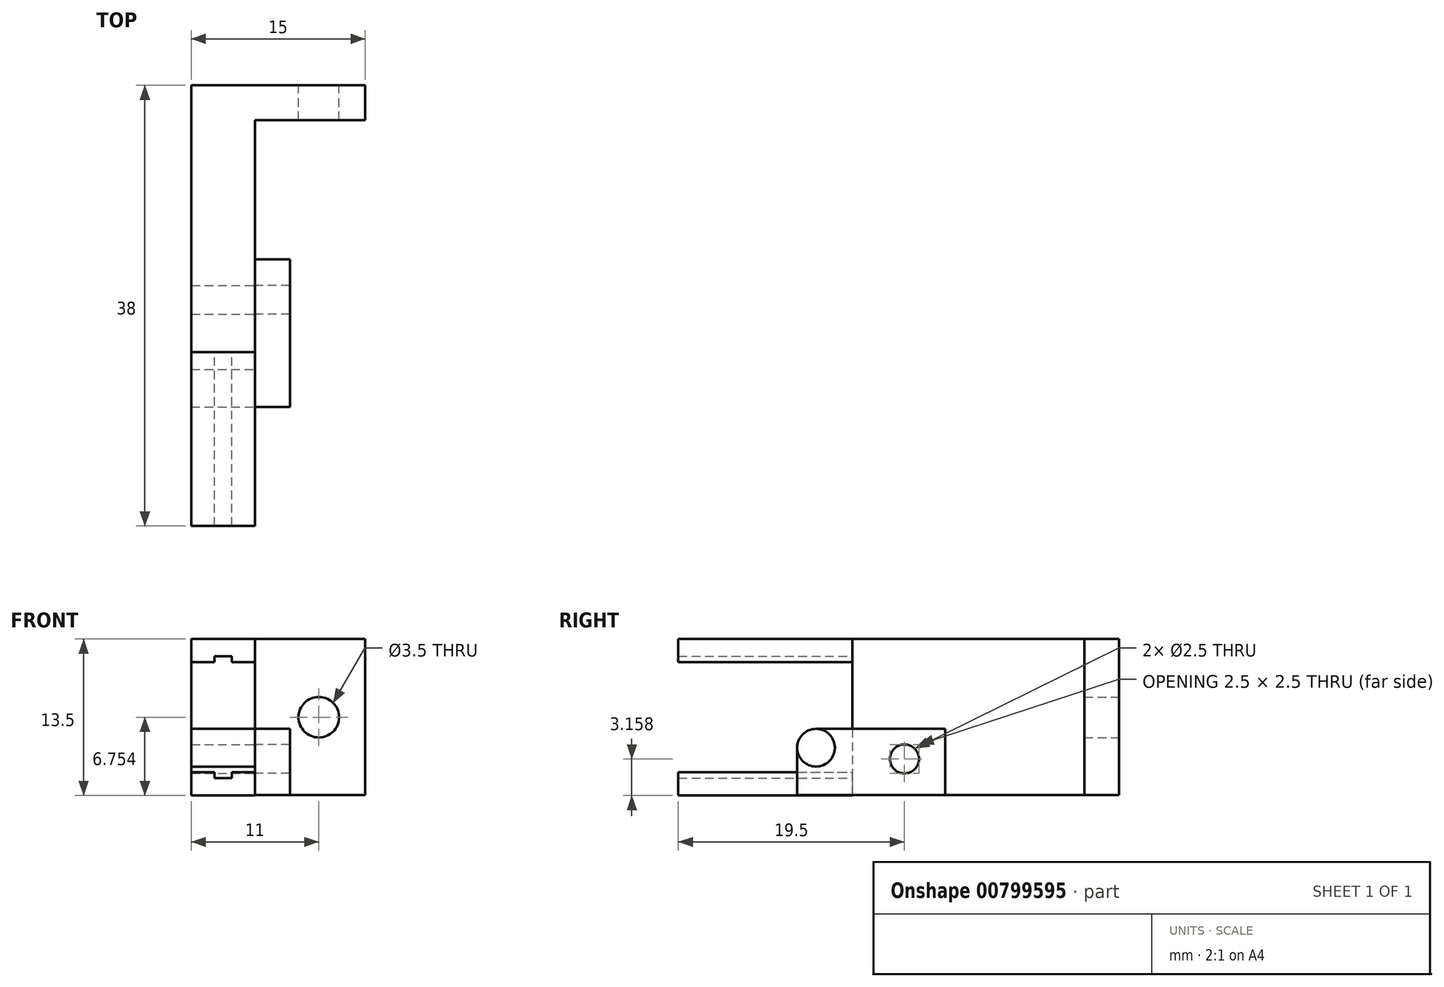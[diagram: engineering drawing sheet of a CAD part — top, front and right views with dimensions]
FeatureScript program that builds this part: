
annotation { "Feature Type Name" : "Feature", "Feature Type Description" : "" }
export const myFeature = defineFeature(function(context is Context, id is Id, definition is map)
    precondition{}
    {
        {
            var Q0;
            Q0=qCreatedBy(makeId("Right.planeOp"),FACE);
            cPlane(context, id + "F0", {"entities" : qUnion([Q0]), "cplaneType" : CPlaneType.OFFSET, "offset" : 2.75 * mm, "width" : 150 * mm, "height" : 150 * mm});
        }
        {
            var Q0;
            Q0=qCreatedBy(makeId("Front.planeOp"),FACE);
            var sketch = newSketch(context, id + "F1", { "sketchPlane" : qUnion([Q0])});
            skLineSegment(sketch, "E0", {"start": v(-0.75, 8) * mm, "end": v(-0.75, 7.5) * mm});
            skLineSegment(sketch, "E1", {"start": v(-0.75, 7.5) * mm, "end": v(-2.75, 7.5) * mm});
            skLineSegment(sketch, "E2", {"start": v(-2.75, 7.5) * mm, "end": v(-2.75, 9.5) * mm});
            skLineSegment(sketch, "E3", {"start": v(-2.75, 9.5) * mm, "end": v(2.75, 9.5) * mm});
            skLineSegment(sketch, "E4", {"start": v(2.75, 9.5) * mm, "end": v(2.75, 7.5) * mm});
            skLineSegment(sketch, "E5", {"start": v(2.75, 7.5) * mm, "end": v(0.75, 7.5) * mm});
            skLineSegment(sketch, "E6", {"start": v(0.75, 7.5) * mm, "end": v(0.75, 8) * mm});
            skLineSegment(sketch, "E7", {"start": v(0.75, 8) * mm, "end": v(-0.75, 8) * mm});
            skLineSegment(sketch, "E8.MirrorCS", {"start": v(0.75, -2.5) * mm, "end": v(-0.75, -2.5) * mm});
            skLineSegment(sketch, "E9.MirrorCS", {"start": v(0.75, -2) * mm, "end": v(0.75, -2.5) * mm});
            skLineSegment(sketch, "E10.MirrorCS", {"start": v(2.75, -4) * mm, "end": v(2.75, -2) * mm});
            skLineSegment(sketch, "E11.MirrorCS", {"start": v(-2.75, -4) * mm, "end": v(2.75, -4) * mm});
            skLineSegment(sketch, "E12.MirrorCS", {"start": v(2.75, -2) * mm, "end": v(0.75, -2) * mm});
            skLineSegment(sketch, "E13.MirrorCS", {"start": v(-0.75, -2.5) * mm, "end": v(-0.75, -2) * mm});
            skLineSegment(sketch, "E14.MirrorCS", {"start": v(-2.75, -2) * mm, "end": v(-2.75, -4) * mm});
            skLineSegment(sketch, "E15.MirrorCS", {"start": v(-0.75, -2) * mm, "end": v(-2.75, -2) * mm});
            skSolve(sketch);
        }
        {
            var Q0;
            Q0 = qSketchRegion(id + "F1", true);
            extrude(context, id + "F2", {"entities" : qUnion([Q0]), "depth" : 15 * mm, "offsetDistance" : 25 * mm});
        }
        {
            var Q0;
            Q0=qCreatedBy(makeId("Front.planeOp"),FACE);
            var sketch = newSketch(context, id + "F3", { "sketchPlane" : qUnion([Q0])});
            skLineSegment(sketch, "E16.bottom", {"start": v(-2.74, 9.5) * mm, "end": v(2.75, 9.5) * mm});
            skLineSegment(sketch, "E16.top", {"start": v(-2.74, -3.96) * mm, "end": v(2.75, -3.96) * mm});
            skLineSegment(sketch, "E16.left", {"start": v(-2.74, 9.5) * mm, "end": v(-2.74, -3.96) * mm});
            skLineSegment(sketch, "E16.right", {"start": v(2.75, 9.5) * mm, "end": v(2.75, -3.96) * mm});
            skSolve(sketch);
        }
        {
            var Q0;
            Q0 = qSketchRegion(id + "F3", true);
            extrude(context, id + "F4", {"entities" : qUnion([Q0]), "oppositeDirection" : true, "depth" : 20 * mm, "offsetDistance" : 25 * mm});
        }
        {
            var Q0;
            Q0=qCreatedBy(id+"F0.planeOp",FACE);
            var sketch = newSketch(context, id + "F5", { "sketchPlane" : qUnion([Q0])});
            skCircle(sketch, "E17", {"center": v(-3.12, 0.12) * mm, "radius": 1.63 * mm});
            skLineSegment(sketch, "E18.bottom", {"start": v(-3.12, 1.75) * mm, "end": v(8, 1.75) * mm});
            skLineSegment(sketch, "E18.top", {"start": v(-4.75, -3.96) * mm, "end": v(8, -3.96) * mm});
            skLineSegment(sketch, "E18.left", {"start": v(-4.75, 0.12) * mm, "end": v(-4.75, -3.96) * mm});
            skLineSegment(sketch, "E18.right", {"start": v(8, 1.75) * mm, "end": v(8, -3.96) * mm});
            skPoint(sketch, "E19.visualSharp", {"position": v(-4.75, 1.75) * mm});
            skArc(sketch, "E19.filletArc", {"start": v(-3.12, 1.75) * mm, "mid": v(-4.27, 1.27) * mm, "end": v(-4.75, 0.12) * mm});
            skPoint(sketch, "E20", {"position": v(4.5, -0.84) * mm});
            skSolve(sketch);
        }
        {
            var Q0;
            Q0=sQuery(id+"F5.wireOp",VERTEX,"E20");
            var Q1;
            Q1=makeQuery(id+"F4.opExtrude","SWEPT_BODY",BODY,{"disambiguationData":[OSD([sQuery(id+"F3.wireOp",EDGE,"E16.bottom"),sQuery(id+"F3.wireOp",EDGE,"E16.top"),sQuery(id+"F3.wireOp",EDGE,"E16.left"),sQuery(id+"F3.wireOp",EDGE,"E16.right")])]});
            hole(context, id + "F6", {"style" : HoleStyle.SIMPLE, "endStyle" : HoleEndStyle.THROUGH, "holeDiameter" : 2.5 * mm, "majorDiameter" : 5 * mm, "isTappedThrough" : true, "tappedDepth" : 12 * mm, "tapClearance" : 3, "locations" : qUnion([Q0]), "scope" : qUnion([Q1])});
        }
        {
            var Q0;
            {var subQ0=sQuery(id+"F5.wireOp",EDGE,"E17");var subQ1=makeQuery(id+"F5.imprint","INTERSECT",VERTEX,{"derivedFrom":[subQ0,sQuery(id+"F5.wireOp",EDGE,"E18.bottom")]});Q0=makeQuery(id+"F5.imprint","IMPRINT",FACE,{"disambiguationData":[TD([[makeQuery(id+"F5.imprint","IMPRINT",EDGE,{"disambiguationData":[TD([[subQ1,-1.0]])],"derivedFrom":subQ0}),1.0]])]});}
            extrude(context, id + "F7", {"entities" : qUnion([Q0]), "depth" : -5.5 * mm, "offsetDistance" : 25 * mm});
        }
        {
            var Q0;
            Q0 = qSketchRegion(id + "F5", true);
            extrude(context, id + "F8", {"entities" : qUnion([Q0]), "depth" : 3 * mm, "offsetDistance" : 25 * mm});
        }
        {
            var Q0;
            Q0=sQuery(id+"F5.wireOp",VERTEX,"E20");
            var Q1;
            Q1=makeQuery(id+"F8.opExtrude","SWEPT_BODY",BODY,{"disambiguationData":[OSD([sQuery(id+"F5.wireOp",EDGE,"E17"),sQuery(id+"F5.wireOp",EDGE,"E18.bottom"),sQuery(id+"F5.wireOp",EDGE,"E18.top"),sQuery(id+"F5.wireOp",EDGE,"E18.left"),sQuery(id+"F5.wireOp",EDGE,"E18.right")])]});
            hole(context, id + "F9", {"style" : HoleStyle.SIMPLE, "endStyle" : HoleEndStyle.THROUGH, "oppositeDirection" : true, "holeDiameter" : 2.5 * mm, "majorDiameter" : 5 * mm, "isTappedThrough" : true, "tappedDepth" : 12 * mm, "tapClearance" : 3, "locations" : qUnion([Q0]), "scope" : qUnion([Q1])});
        }
        {
            var Q0;
            Q0=qCreatedBy(makeId("Right.planeOp"),FACE);
            cPlane(context, id + "F10", {"entities" : qUnion([Q0]), "cplaneType" : CPlaneType.OFFSET, "offset" : 2.75 * mm, "oppositeDirection" : true, "width" : 150 * mm, "height" : 150 * mm});
        }
        {
            var Q0;
            Q0=qCreatedBy(id+"F10.planeOp",FACE);
            var sketch = newSketch(context, id + "F11", { "sketchPlane" : qUnion([Q0])});
            skLineSegment(sketch, "E21.bottom", {"start": v(20, 9.5) * mm, "end": v(23, 9.5) * mm});
            skLineSegment(sketch, "E21.top", {"start": v(20, -3.96) * mm, "end": v(23, -3.96) * mm});
            skLineSegment(sketch, "E21.left", {"start": v(20, 9.5) * mm, "end": v(20, -3.96) * mm});
            skLineSegment(sketch, "E21.right", {"start": v(23, 9.5) * mm, "end": v(23, -3.96) * mm});
            skSolve(sketch);
        }
        {
            var Q0;
            Q0 = qSketchRegion(id + "F11", true);
            extrude(context, id + "F12", {"entities" : qUnion([Q0]), "operationType" : NewBodyOperationType.ADD, "depth" : 15 * mm, "offsetDistance" : 25 * mm});
        }
        {
            var Q0;
            Q0=makeQuery(id+"F12.opExtrude","SWEPT_FACE",FACE,{"disambiguationData":[OSD([sQuery(id+"F11.wireOp",EDGE,"E21.right")])]});
            cPlane(context, id + "F13", {"entities" : qUnion([Q0]), "cplaneType" : CPlaneType.OFFSET, "offset" : 0 * mm, "width" : 150 * mm, "height" : 150 * mm});
        }
        {
            var Q0;
            Q0=qCreatedBy(id+"F13.planeOp",FACE);
            var sketch = newSketch(context, id + "F14", { "sketchPlane" : qUnion([Q0])});
            skPoint(sketch, "E22", {"position": v(-8.25, 2.75) * mm});
            skSolve(sketch);
        }
        {
            var Q0;
            Q0=sQuery(id+"F14.wireOp",VERTEX,"E22");
            var Q1;
            Q1=makeQuery(id+"F4.opExtrude","SWEPT_BODY",BODY,{"disambiguationData":[OSD([sQuery(id+"F3.wireOp",EDGE,"E16.bottom"),sQuery(id+"F3.wireOp",EDGE,"E16.top"),sQuery(id+"F3.wireOp",EDGE,"E16.left"),sQuery(id+"F3.wireOp",EDGE,"E16.right")])]});
            hole(context, id + "F15", {"style" : HoleStyle.SIMPLE, "endStyle" : HoleEndStyle.THROUGH, "holeDiameter" : 3.5 * mm, "majorDiameter" : 5 * mm, "isTappedThrough" : true, "tappedDepth" : 12 * mm, "tapClearance" : 3, "locations" : qUnion([Q0]), "scope" : qUnion([Q1])});
        }
    });
